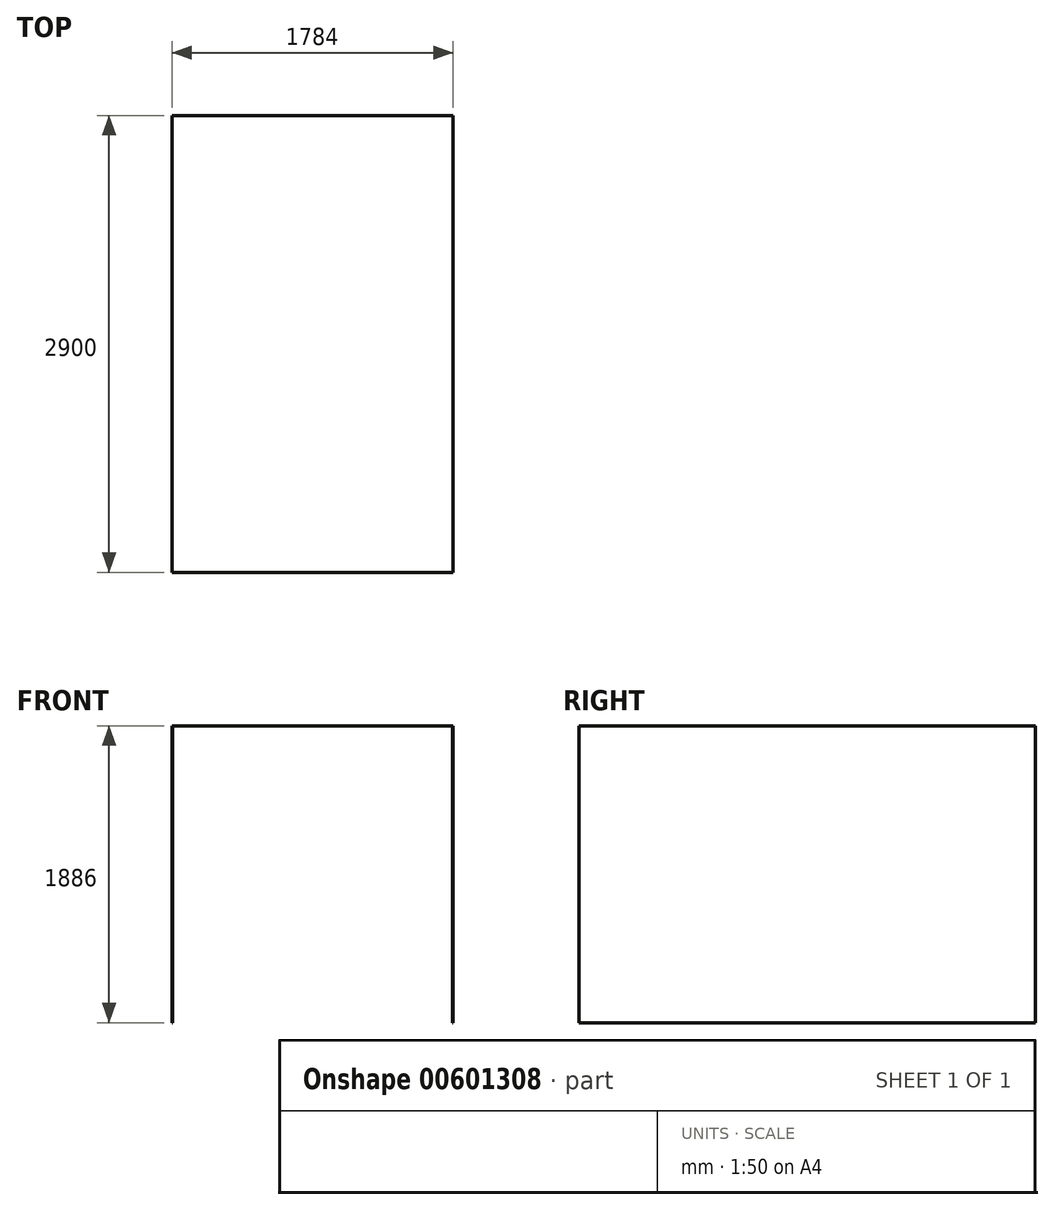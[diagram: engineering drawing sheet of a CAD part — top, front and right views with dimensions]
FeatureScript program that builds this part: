
annotation { "Feature Type Name" : "Feature", "Feature Type Description" : "" }
export const myFeature = defineFeature(function(context is Context, id is Id, definition is map)
    precondition{}
    {
        {
            var Q0;
            Q0=qCreatedBy(makeId("Top.planeOp"),FACE);
            var sketch = newSketch(context, id + "F0", { "sketchPlane" : qUnion([Q0])});
            skLineSegment(sketch, "E0.bottom", {"start": v(0, 0) * mm, "end": v(1784, 0) * mm});
            skLineSegment(sketch, "E0.top", {"start": v(0, 2900) * mm, "end": v(1784, 2900) * mm});
            skLineSegment(sketch, "E0.left", {"start": v(0, 0) * mm, "end": v(0, 2900) * mm});
            skLineSegment(sketch, "E0.right", {"start": v(1784, 0) * mm, "end": v(1784, 2900) * mm});
            skSolve(sketch);
        }
        {
            var Q0;
            Q0 = qSketchRegion(id + "F0", true);
            extrude(context, id + "F1", {"entities" : qUnion([Q0]), "depth" : 1886 * mm, "offsetDistance" : 25 * mm});
        }
        {
            var Q0;
            Q0=makeQuery(id+"F1.opExtrude","SWEPT_FACE",FACE,{"disambiguationData":[OSD([sQuery(id+"F0.wireOp",EDGE,"E0.bottom")])]});
            var Q1;
            Q1=makeQuery(id+"F1.opExtrude","SWEPT_FACE",FACE,{"disambiguationData":[OSD([sQuery(id+"F0.wireOp",EDGE,"E0.top")])]});
            var Q2;
            Q2=makeQuery(id+"F1.opExtrude","CAP_FACE",FACE,{"disambiguationData":[OSD([sQuery(id+"F0.wireOp",EDGE,"E0.bottom"),sQuery(id+"F0.wireOp",EDGE,"E0.top"),sQuery(id+"F0.wireOp",EDGE,"E0.left"),sQuery(id+"F0.wireOp",EDGE,"E0.right")])],"isStart":true});
            shell(context, id + "F2", {"entities" : qUnion([Q0, Q1, Q2]), "thickness" : 2.5 * mm});
        }
    });
